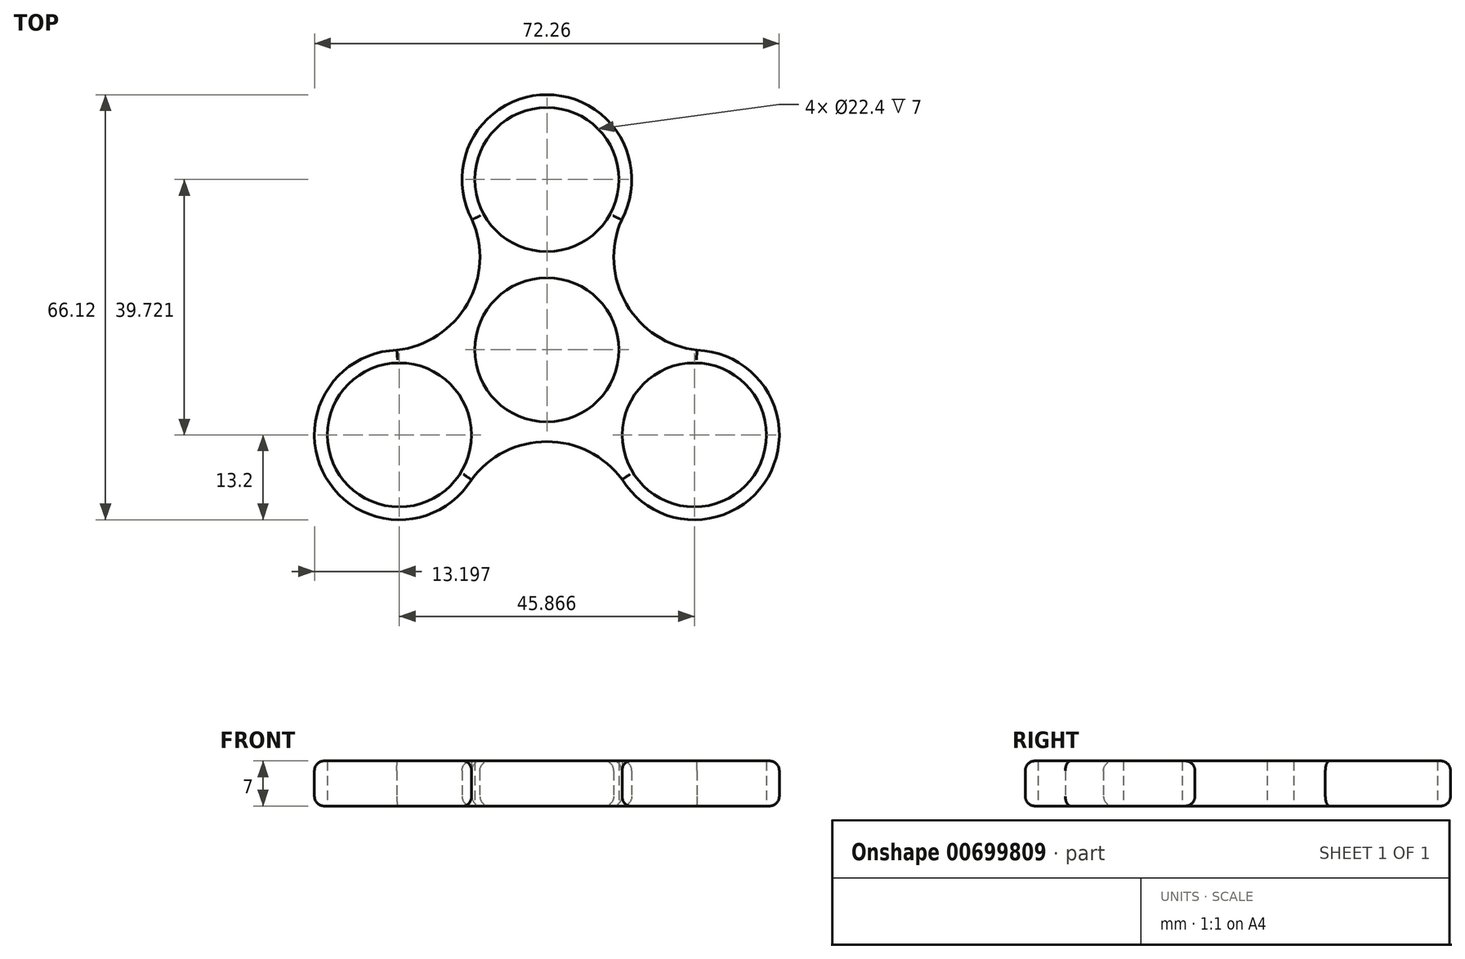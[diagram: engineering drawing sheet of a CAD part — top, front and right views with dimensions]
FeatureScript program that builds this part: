
annotation { "Feature Type Name" : "Feature", "Feature Type Description" : "" }
export const myFeature = defineFeature(function(context is Context, id is Id, definition is map)
    precondition{}
    {
        {
            var Q0;
            Q0=qCreatedBy(makeId("Top.planeOp"),FACE);
            var sketch = newSketch(context, id + "F0", { "sketchPlane" : qUnion([Q0])});
            skCircle(sketch, "E0", {"center": v(0, 0) * mm, "radius": 11.2 * mm});
            skCircle(sketch, "E1", {"center": v(0, 26.48) * mm, "radius": 11.2 * mm});
            skArc(sketch, "E2", {"start": v(11.62, 20.22) * mm, "mid": v(0.02, 39.68) * mm, "end": v(-11.64, 20.25) * mm});
            skArc(sketch, "E3.1.0", {"start": v(-23.32, -0.05) * mm, "mid": v(-34.37, -19.82) * mm, "end": v(-11.72, -20.2) * mm});
            skArc(sketch, "E3.2.0", {"start": v(11.7, -20.17) * mm, "mid": v(34.35, -19.86) * mm, "end": v(23.36, -0.05) * mm});
            skCircle(sketch, "E4.1.0", {"center": v(-22.93, -13.24) * mm, "radius": 11.2 * mm});
            skCircle(sketch, "E4.2.0", {"center": v(22.93, -13.24) * mm, "radius": 11.2 * mm});
            skArc(sketch, "E5", {"start": v(12.12, 21.26) * mm, "mid": v(12.09, 7.62) * mm, "end": v(23.36, -0.05) * mm});
            skArc(sketch, "E6.1.0", {"start": v(-24.47, -0.13) * mm, "mid": v(-12.65, 6.66) * mm, "end": v(-11.64, 20.25) * mm});
            skArc(sketch, "E6.2.0", {"start": v(12.35, -21.13) * mm, "mid": v(0.56, -14.28) * mm, "end": v(-11.72, -20.2) * mm});
            skSolve(sketch);
        }
        {
            var Q0;
            Q0 = qSketchRegion(id + "F0", true);
            extrude(context, id + "F1", {"entities" : qUnion([Q0]), "depth" : 7 * mm, "offsetDistance" : 25 * mm});
        }
        {
            var Q0;
            Q0=makeQuery(id+"F1.opExtrude","CAP_EDGE",EDGE,{"disambiguationData":[OSD([sQuery(id+"F0.wireOp",EDGE,"E3.1.0")])],"isStart":false});
            var Q1;
            Q1=makeQuery(id+"F1.opExtrude","CAP_EDGE",EDGE,{"disambiguationData":[OSD([sQuery(id+"F0.wireOp",EDGE,"E6.2.0")])],"isStart":false});
            var Q2;
            Q2=makeQuery(id+"F1.opExtrude","CAP_EDGE",EDGE,{"disambiguationData":[OSD([sQuery(id+"F0.wireOp",EDGE,"E3.2.0")])],"isStart":false});
            var Q3;
            Q3=makeQuery(id+"F1.opExtrude","CAP_EDGE",EDGE,{"disambiguationData":[OSD([sQuery(id+"F0.wireOp",EDGE,"E5")])],"isStart":false});
            var Q4;
            Q4=makeQuery(id+"F1.opExtrude","CAP_EDGE",EDGE,{"disambiguationData":[OSD([sQuery(id+"F0.wireOp",EDGE,"E2")])],"isStart":false});
            var Q5;
            Q5=makeQuery(id+"F1.opExtrude","CAP_EDGE",EDGE,{"disambiguationData":[OSD([sQuery(id+"F0.wireOp",EDGE,"E6.1.0")])],"isStart":false});
            var Q6;
            Q6=makeQuery(id+"F1.opExtrude","CAP_EDGE",EDGE,{"disambiguationData":[OSD([sQuery(id+"F0.wireOp",EDGE,"E3.2.0")])],"isStart":true});
            var Q7;
            Q7=makeQuery(id+"F1.opExtrude","CAP_EDGE",EDGE,{"disambiguationData":[OSD([sQuery(id+"F0.wireOp",EDGE,"E3.1.0")])],"isStart":true});
            var Q8;
            Q8=makeQuery(id+"F1.opExtrude","CAP_EDGE",EDGE,{"disambiguationData":[OSD([sQuery(id+"F0.wireOp",EDGE,"E6.1.0")])],"isStart":true});
            var Q9;
            Q9=makeQuery(id+"F1.opExtrude","CAP_EDGE",EDGE,{"disambiguationData":[OSD([sQuery(id+"F0.wireOp",EDGE,"E2")])],"isStart":true});
            var Q10;
            Q10=makeQuery(id+"F1.opExtrude","CAP_EDGE",EDGE,{"disambiguationData":[OSD([sQuery(id+"F0.wireOp",EDGE,"E5")])],"isStart":true});
            fillet(context, id + "F2", {"entities" : qUnion([Q0, Q1, Q2, Q3, Q4, Q5, Q6, Q7, Q8, Q9, Q10]), "radius" : 1.5 * mm, "tangentPropagation" : true, "allowEdgeOverflow" : false});
        }
    });
